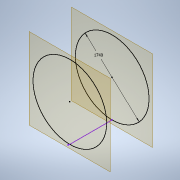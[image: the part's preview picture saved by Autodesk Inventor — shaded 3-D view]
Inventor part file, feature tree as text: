
AUTODESK INVENTOR PART (.ipt)
format: ipt  version: 2021 (Build 250183000, 183)  size: 119,808 bytes
history: native  units: mm
features: other x4, sketch x3, loft x1, shell x1
ambient origin geometry x8: Origin, YZ Plane, XZ Plane, XY Plane, X Axis, Y Axis, Z Axis, Center Point
bodies: Body1 (feature_tree)
feature tree (9):
  other  "Bryła1"
  sketch  "Szkic1"
  other  "Płaszczyzna konstrukcyjna1"
  sketch  "Szkic2"
  sketch  "Szkic 3D2"
  loft  "Wyciągnięcie złożone1"
  shell  "Skorupa1"  Thickness=1000.0mm
  other  "Punkt konstrukcyjny1"
  other  "Punkt konstrukcyjny2"
